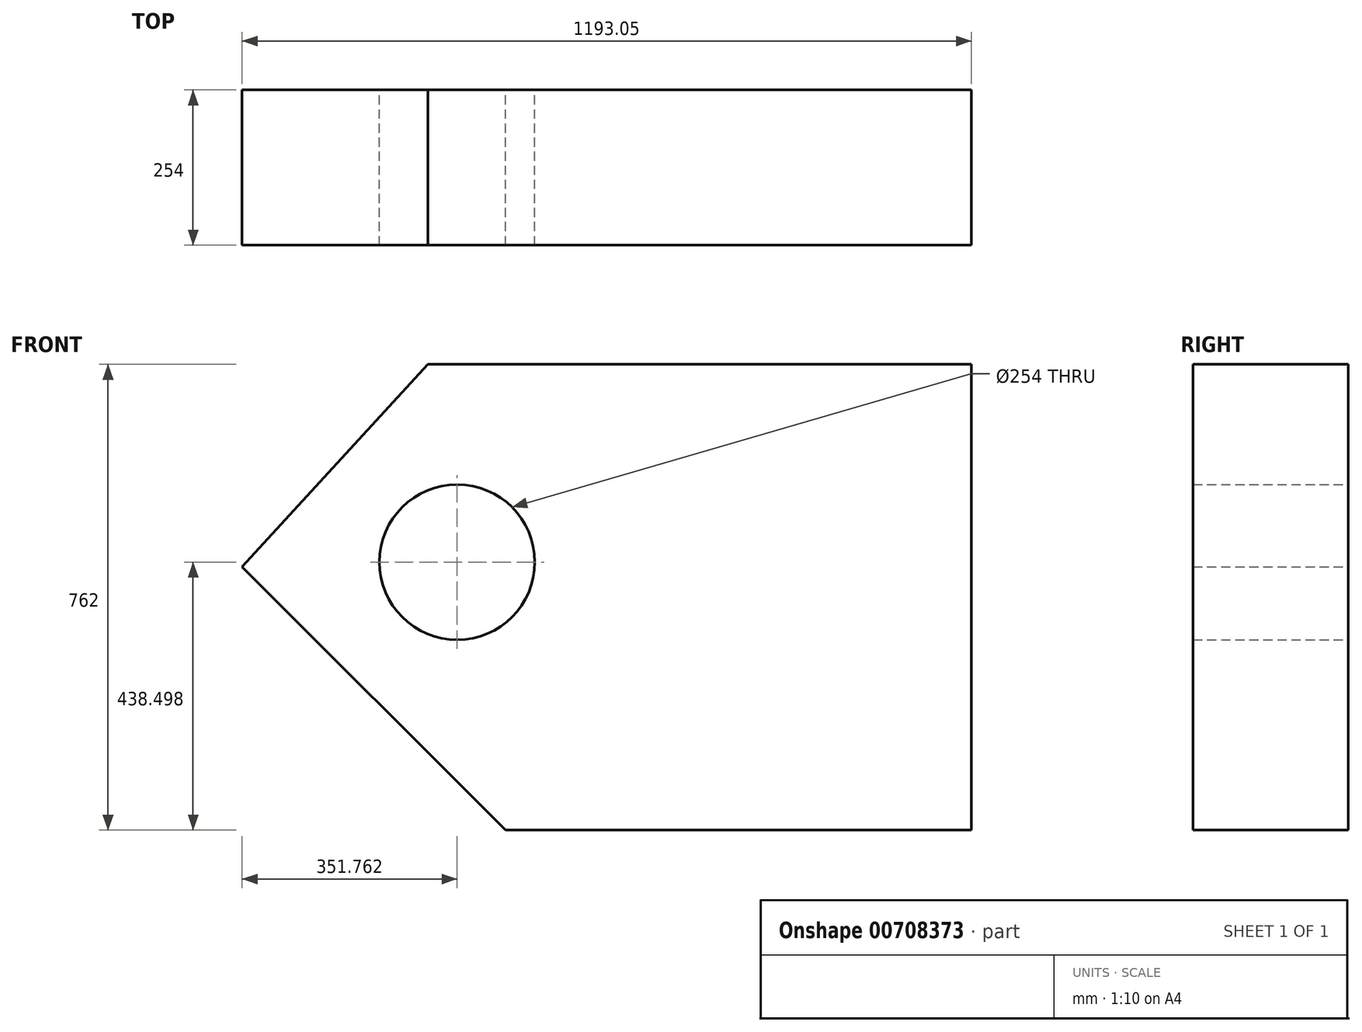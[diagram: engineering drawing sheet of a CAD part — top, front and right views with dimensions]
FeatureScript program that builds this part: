
annotation { "Feature Type Name" : "Feature", "Feature Type Description" : "" }
export const myFeature = defineFeature(function(context is Context, id is Id, definition is map)
    precondition{}
    {
        {
            var Q0;
            Q0=qCreatedBy(makeId("Front.planeOp"),FACE);
            var sketch = newSketch(context, id + "F0", { "sketchPlane" : qUnion([Q0])});
            skLineSegment(sketch, "E0", {"start": v(0, 0) * mm, "end": v(762, 0) * mm});
            skLineSegment(sketch, "E1", {"start": v(0, 0) * mm, "end": v(-431.05, 431.05) * mm});
            skLineSegment(sketch, "E2", {"start": v(762, 0) * mm, "end": v(762, 762) * mm});
            skLineSegment(sketch, "E3", {"start": v(762, 762) * mm, "end": v(-127, 762) * mm});
            skLineSegment(sketch, "E4", {"start": v(-431.05, 431.05) * mm, "end": v(-127, 762) * mm});
            skCircle(sketch, "E5", {"center": v(-79.29, 438.5) * mm, "radius": 127 * mm});
            skSolve(sketch);
        }
        {
            var Q0;
            Q0 = qSketchRegion(id + "F0", true);
            extrude(context, id + "F1", {"entities" : qUnion([Q0]), "depth" : 254 * mm, "offsetDistance" : 25.4 * mm});
        }
    });
